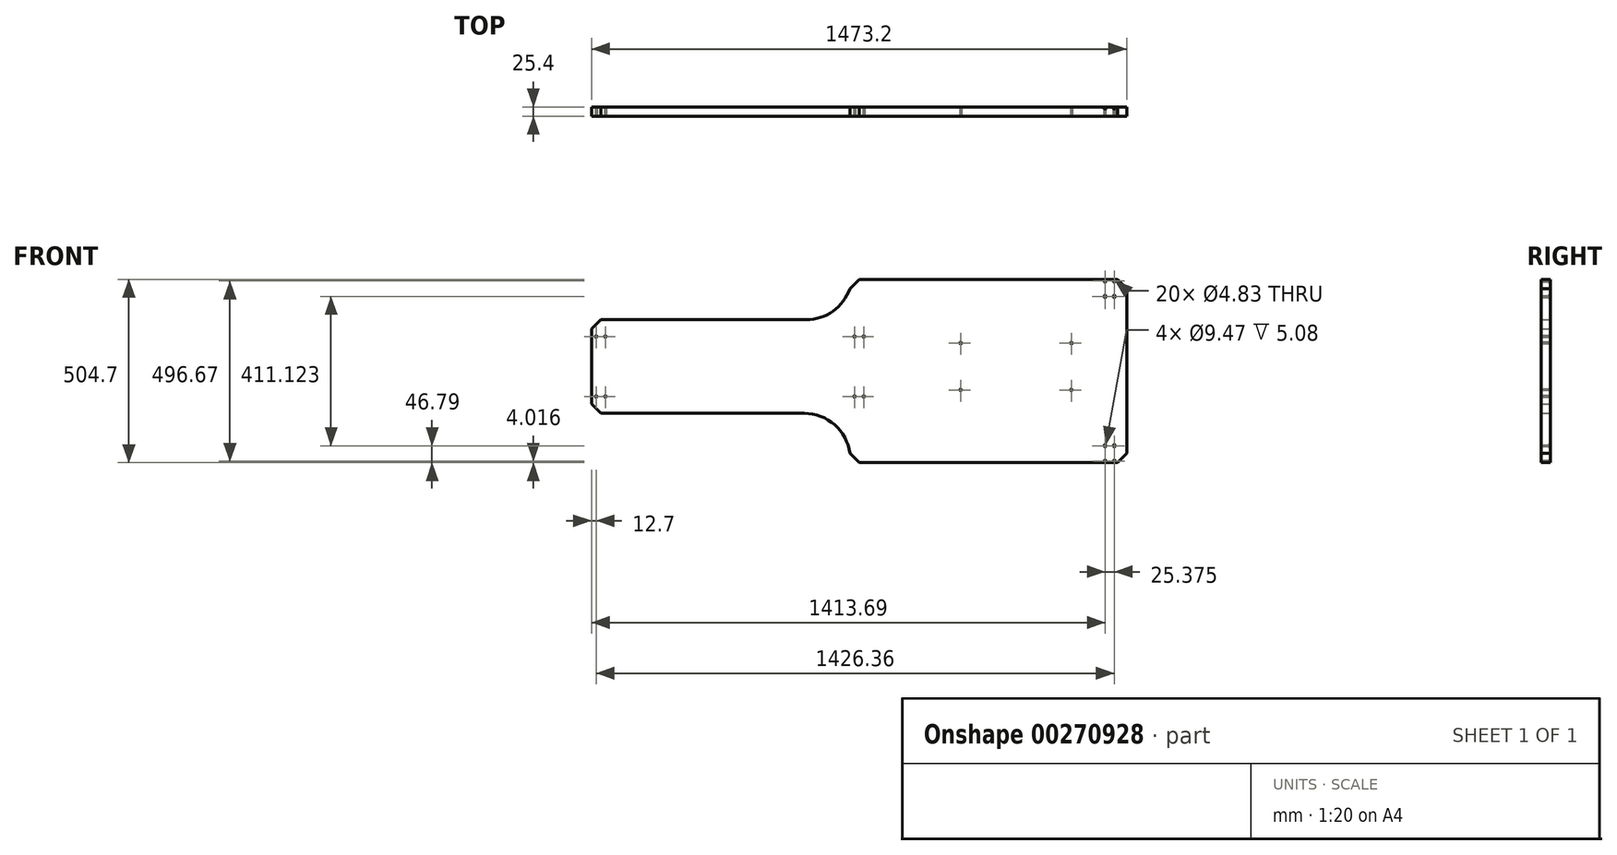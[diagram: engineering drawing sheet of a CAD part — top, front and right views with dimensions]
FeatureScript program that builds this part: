
annotation { "Feature Type Name" : "Feature", "Feature Type Description" : "" }
export const myFeature = defineFeature(function(context is Context, id is Id, definition is map)
    precondition{}
    {
        {
            var Q0;
            Q0=qCreatedBy(makeId("Front.planeOp"),FACE);
            var sketch = newSketch(context, id + "F0", { "sketchPlane" : qUnion([Q0])});
            skLineSegment(sketch, "E0", {"start": v(-1473.2, 384.96) * mm, "end": v(-1473.2, 177.8) * mm});
            skLineSegment(sketch, "E1", {"start": v(-1447.8, 410.36) * mm, "end": v(-881.95, 410.36) * mm});
            skLineSegment(sketch, "E2", {"start": v(-1447.8, 152.4) * mm, "end": v(-887.95, 152.4) * mm});
            skLineSegment(sketch, "E3", {"start": v(-736.6, 16.33) * mm, "end": v(-25.4, 16.33) * mm});
            skLineSegment(sketch, "E4", {"start": v(-736.6, 521.03) * mm, "end": v(-25.4, 521.03) * mm});
            skPoint(sketch, "E5.visualSharp", {"position": v(-762, 410.36) * mm});
            skArc(sketch, "E5.filletArc", {"start": v(-881.95, 410.36) * mm, "mid": v(-808.36, 433.85) * mm, "end": v(-762, 495.63) * mm});
            skPoint(sketch, "E6.visualSharp", {"position": v(-762, 152.4) * mm});
            skArc(sketch, "E6.filletArc", {"start": v(-762, 41.73) * mm, "mid": v(-804.12, 120.8) * mm, "end": v(-887.95, 152.4) * mm});
            skLineSegment(sketch, "E7", {"start": v(-736.6, 521.03) * mm, "end": v(-762, 495.63) * mm});
            skPoint(sketch, "E8.orphan", {"position": v(-762, 521.03) * mm});
            skLineSegment(sketch, "E9", {"start": v(-736.6, 16.33) * mm, "end": v(-762, 41.73) * mm});
            skPoint(sketch, "E10.orphan", {"position": v(-762, 16.33) * mm});
            skLineSegment(sketch, "E11", {"start": v(-25.4, 16.33) * mm, "end": v(0, 41.73) * mm});
            skLineSegment(sketch, "E12", {"start": v(-1473.2, 384.96) * mm, "end": v(-1447.8, 410.36) * mm});
            skLineSegment(sketch, "E13", {"start": v(-1447.8, 152.4) * mm, "end": v(-1473.2, 177.8) * mm});
            skLineSegment(sketch, "E14", {"start": v(0, 495.63) * mm, "end": v(0, 41.73) * mm});
            skPoint(sketch, "E15.endSnap0", {"position": v(0, 140.7) * mm});
            skPoint(sketch, "E16.orphan", {"position": v(-1473.2, 0) * mm});
            skLineSegment(sketch, "E17", {"start": v(-1473.2, 281.38) * mm, "end": v(-1473.2, 344.88) * mm});
            skLineSegment(sketch, "E18", {"start": v(-1473.2, 281.38) * mm, "end": v(-1473.2, 217.88) * mm});
            skLineSegment(sketch, "E19", {"start": v(-1473.2, 344.88) * mm, "end": v(-1473.2, 382.98) * mm});
            skLineSegment(sketch, "E20", {"start": v(-1473.2, 382.98) * mm, "end": v(-1422.4, 382.98) * mm});
            skLineSegment(sketch, "E21", {"start": v(-1473.2, 217.88) * mm, "end": v(-1473.2, 179.78) * mm});
            skLineSegment(sketch, "E22", {"start": v(-1473.2, 179.78) * mm, "end": v(-1422.4, 179.78) * mm});
            skLineSegment(sketch, "E23", {"start": v(-1473.2, 344.88) * mm, "end": v(-711.2, 344.88) * mm});
            skLineSegment(sketch, "E24", {"start": v(-711.2, 344.88) * mm, "end": v(-711.2, 217.88) * mm});
            skLineSegment(sketch, "E25", {"start": v(-711.2, 217.88) * mm, "end": v(-1473.2, 217.88) * mm});
            skLineSegment(sketch, "E26", {"start": v(-1422.4, 179.78) * mm, "end": v(-1422.4, 217.88) * mm});
            skLineSegment(sketch, "E27", {"start": v(-1422.4, 382.98) * mm, "end": v(-1422.4, 344.88) * mm});
            skLineSegment(sketch, "E28", {"start": v(-1473.2, 344.88) * mm, "end": v(-1460.5, 344.88) * mm});
            skLineSegment(sketch, "E29", {"start": v(-1460.5, 344.88) * mm, "end": v(-1460.5, 363.93) * mm});
            skLineSegment(sketch, "E30", {"start": v(-1422.4, 344.88) * mm, "end": v(-1435.1, 344.88) * mm});
            skLineSegment(sketch, "E31", {"start": v(-1435.1, 344.88) * mm, "end": v(-1435.1, 363.93) * mm});
            skLineSegment(sketch, "E32", {"start": v(-1460.5, 217.88) * mm, "end": v(-1460.5, 198.83) * mm});
            skLineSegment(sketch, "E33", {"start": v(-1435.1, 217.88) * mm, "end": v(-1435.1, 198.83) * mm});
            skLineSegment(sketch, "E34", {"start": v(-711.2, 217.88) * mm, "end": v(-723.9, 217.88) * mm});
            skLineSegment(sketch, "E35", {"start": v(-723.9, 217.88) * mm, "end": v(-723.9, 198.83) * mm});
            skLineSegment(sketch, "E36", {"start": v(-762, 198.83) * mm, "end": v(-762, 217.88) * mm});
            skLineSegment(sketch, "E37", {"start": v(-711.2, 344.88) * mm, "end": v(-723.9, 344.88) * mm});
            skLineSegment(sketch, "E38", {"start": v(-723.9, 344.88) * mm, "end": v(-762, 344.88) * mm});
            skLineSegment(sketch, "E39", {"start": v(-762, 344.88) * mm, "end": v(-762, 363.93) * mm});
            skLineSegment(sketch, "E40", {"start": v(-723.9, 344.88) * mm, "end": v(-723.9, 363.93) * mm});
            skLineSegment(sketch, "E41", {"start": v(0, 495.63) * mm, "end": v(-25.4, 521.03) * mm});
            skSolve(sketch);
        }
        {
            var Q0;
            Q0=makeQuery(id+"F0.imprint","IMPRINT",FACE,{"disambiguationData":[TD([[makeQuery(id+"F0.imprint","IMPRINT",EDGE,{"derivedFrom":sQuery(id+"F0.wireOp",EDGE,"E0")}),1.0]])]});
            extrude(context, id + "F1", {"entities" : qUnion([Q0]), "depth" : 12.7 * mm});
        }
        {
            var Q0;
            Q0=makeQuery(id+"F1.opExtrude","CAP_FACE",FACE,{"disambiguationData":[OSD([sQuery(id+"F0.wireOp",EDGE,"E0"),sQuery(id+"F0.wireOp",EDGE,"E1"),sQuery(id+"F0.wireOp",EDGE,"E2"),sQuery(id+"F0.wireOp",EDGE,"E3"),sQuery(id+"F0.wireOp",EDGE,"E4"),sQuery(id+"F0.wireOp",EDGE,"E5.filletArc"),sQuery(id+"F0.wireOp",EDGE,"E6.filletArc"),sQuery(id+"F0.wireOp",EDGE,"E7"),sQuery(id+"F0.wireOp",EDGE,"E9"),sQuery(id+"F0.wireOp",EDGE,"E11"),sQuery(id+"F0.wireOp",EDGE,"2SLSGWGz-MLWY-dJ0c-EU9p-pr2KKDG8ahuz"),sQuery(id+"F0.wireOp",EDGE,"E12"),sQuery(id+"F0.wireOp",EDGE,"E13"),sQuery(id+"F0.wireOp",EDGE,"E14"),sQuery(id+"F0.wireOp",EDGE,"1ipnpV95-zsMA-DrG2-5ojF-kC9brwyhWKc4")])],"isStart":false});
            var sketch = newSketch(context, id + "F2", { "sketchPlane" : qUnion([Q0])});
            skLineSegment(sketch, "E42", {"start": v(-25.4, 16.33) * mm, "end": v(0, 0) * mm});
            skLineSegment(sketch, "E43", {"start": v(0, 0) * mm, "end": v(0, 562.76) * mm});
            skLineSegment(sketch, "E44", {"start": v(0, 562.76) * mm, "end": v(-736.6, 521.03) * mm});
            skLineSegment(sketch, "E45", {"start": v(0, 562.76) * mm, "end": v(0, 268.68) * mm});
            skLineSegment(sketch, "E46", {"start": v(0, 0) * mm, "end": v(0, 268.68) * mm});
            skLineSegment(sketch, "E47", {"start": v(0, 0) * mm, "end": v(0, 134.34) * mm});
            skLineSegment(sketch, "E48", {"start": v(0, 134.34) * mm, "end": v(-152.4, 134.34) * mm});
            skLineSegment(sketch, "E49", {"start": v(-152.4, 134.34) * mm, "end": v(-457.2, 134.34) * mm});
            skLineSegment(sketch, "E50", {"start": v(0, 562.76) * mm, "end": v(0, 415.72) * mm});
            skLineSegment(sketch, "E51", {"start": v(0, 415.72) * mm, "end": v(-152.4, 415.72) * mm});
            skLineSegment(sketch, "E52", {"start": v(-152.4, 415.72) * mm, "end": v(-457.2, 415.72) * mm});
            skPoint(sketch, "E53", {"position": v(-457.2, 415.72) * mm});
            skPoint(sketch, "E54", {"position": v(-152.4, 415.72) * mm});
            skPoint(sketch, "E55", {"position": v(-457.2, 134.34) * mm});
            skPoint(sketch, "E56", {"position": v(-152.4, 134.34) * mm});
            skSolve(sketch);
        }
        {
            var Q0;
            Q0=sQuery(id+"F2.wireOp",VERTEX,"E53");
            var Q1;
            Q1=sQuery(id+"F2.wireOp",VERTEX,"E54");
            var Q2;
            Q2=sQuery(id+"F2.wireOp",VERTEX,"E56");
            var Q3;
            Q3=sQuery(id+"F2.wireOp",VERTEX,"E55");
            var Q4;
            Q4=makeQuery(id+"F1.opExtrude","SWEPT_BODY",BODY,{"disambiguationData":[OSD([sQuery(id+"F0.wireOp",EDGE,"E0"),sQuery(id+"F0.wireOp",EDGE,"E1"),sQuery(id+"F0.wireOp",EDGE,"E2"),sQuery(id+"F0.wireOp",EDGE,"E3"),sQuery(id+"F0.wireOp",EDGE,"E4"),sQuery(id+"F0.wireOp",EDGE,"E5.filletArc"),sQuery(id+"F0.wireOp",EDGE,"E6.filletArc"),sQuery(id+"F0.wireOp",EDGE,"E7"),sQuery(id+"F0.wireOp",EDGE,"E9"),sQuery(id+"F0.wireOp",EDGE,"E11"),sQuery(id+"F0.wireOp",EDGE,"2SLSGWGz-MLWY-dJ0c-EU9p-pr2KKDG8ahuz"),sQuery(id+"F0.wireOp",EDGE,"E12"),sQuery(id+"F0.wireOp",EDGE,"E13"),sQuery(id+"F0.wireOp",EDGE,"E14"),sQuery(id+"F0.wireOp",EDGE,"1ipnpV95-zsMA-DrG2-5ojF-kC9brwyhWKc4")])]});
            hole(context, id + "F3", {"style" : HoleStyle.SIMPLE, "endStyle" : HoleEndStyle.THROUGH, "holeDiameter" : 4.83 * mm, "tappedDepth" : 12.7 * mm, "tapClearance" : 3, "locations" : qUnion([Q0, Q1, Q2, Q3]), "scope" : qUnion([Q4])});
        }
        {
            var Q0;
            Q0 = qSketchRegion(id + "F0", true);
            extrude(context, id + "F4", {"entities" : qUnion([Q0]), "operationType" : NewBodyOperationType.ADD, "depth" : 25.4 * mm});
        }
        {
            var Q0;
            Q0=makeQuery(id+"F4.opExtrude","CAP_FACE",FACE,{"disambiguationData":[OSD([sQuery(id+"F0.wireOp",EDGE,"E0"),sQuery(id+"F0.wireOp",EDGE,"E1"),sQuery(id+"F0.wireOp",EDGE,"E2"),sQuery(id+"F0.wireOp",EDGE,"E3"),sQuery(id+"F0.wireOp",EDGE,"E4"),sQuery(id+"F0.wireOp",EDGE,"E5.filletArc"),sQuery(id+"F0.wireOp",EDGE,"E6.filletArc"),sQuery(id+"F0.wireOp",EDGE,"E7"),sQuery(id+"F0.wireOp",EDGE,"E9"),sQuery(id+"F0.wireOp",EDGE,"E11"),sQuery(id+"F0.wireOp",EDGE,"2SLSGWGz-MLWY-dJ0c-EU9p-pr2KKDG8ahuz"),sQuery(id+"F0.wireOp",EDGE,"E12"),sQuery(id+"F0.wireOp",EDGE,"E13"),sQuery(id+"F0.wireOp",EDGE,"E14"),sQuery(id+"F0.wireOp",EDGE,"1ipnpV95-zsMA-DrG2-5ojF-kC9brwyhWKc4"),sQuery(id+"F0.wireOp",EDGE,"E17"),sQuery(id+"F0.wireOp",EDGE,"E18"),sQuery(id+"F0.wireOp",EDGE,"E19"),sQuery(id+"F0.wireOp",EDGE,"E21")])],"isStart":false});
            var sketch = newSketch(context, id + "F5", { "sketchPlane" : qUnion([Q0])});
            skLineSegment(sketch, "E57", {"start": v(-1473.2, 281.38) * mm, "end": v(-711.2, 281.38) * mm});
            skLineSegment(sketch, "E58", {"start": v(-711.2, 281.38) * mm, "end": v(-711.2, 217.88) * mm});
            skLineSegment(sketch, "E59", {"start": v(-711.2, 217.88) * mm, "end": v(-723.9, 217.88) * mm});
            skLineSegment(sketch, "E60", {"start": v(-723.9, 217.88) * mm, "end": v(-723.9, 198.83) * mm});
            skLineSegment(sketch, "E61", {"start": v(-1473.2, 281.38) * mm, "end": v(-1473.2, 217.88) * mm});
            skLineSegment(sketch, "E62", {"start": v(-1473.2, 217.88) * mm, "end": v(-1422.4, 217.88) * mm});
            skLineSegment(sketch, "E63", {"start": v(-1422.4, 217.88) * mm, "end": v(-1435.1, 217.88) * mm});
            skPoint(sketch, "E63.endSnap0", {"position": v(-1447.8, 217.88) * mm});
            skLineSegment(sketch, "E64", {"start": v(-1435.1, 217.88) * mm, "end": v(-1435.1, 198.83) * mm});
            skLineSegment(sketch, "E65", {"start": v(-1460.5, 198.83) * mm, "end": v(-1460.5, 217.88) * mm});
            skLineSegment(sketch, "E66", {"start": v(-749.3, 217.88) * mm, "end": v(-749.3, 198.83) * mm});
            skLineSegment(sketch, "E67.MirrorCS", {"start": v(-749.3, 344.88) * mm, "end": v(-749.3, 363.93) * mm});
            skLineSegment(sketch, "E68.MirrorCS", {"start": v(-723.9, 344.88) * mm, "end": v(-723.9, 363.93) * mm});
            skLineSegment(sketch, "E69.MirrorCS", {"start": v(-1435.1, 344.88) * mm, "end": v(-1435.1, 363.93) * mm});
            skLineSegment(sketch, "E70.MirrorCS", {"start": v(-1460.5, 363.93) * mm, "end": v(-1460.5, 344.88) * mm});
            skSolve(sketch);
        }
        {
            var Q0;
            Q0=makeQuery(id+"F4.opExtrude","CAP_FACE",FACE,{"disambiguationData":[OSD([sQuery(id+"F0.wireOp",EDGE,"E0"),sQuery(id+"F0.wireOp",EDGE,"E1"),sQuery(id+"F0.wireOp",EDGE,"E2"),sQuery(id+"F0.wireOp",EDGE,"E3"),sQuery(id+"F0.wireOp",EDGE,"E4"),sQuery(id+"F0.wireOp",EDGE,"E5.filletArc"),sQuery(id+"F0.wireOp",EDGE,"E6.filletArc"),sQuery(id+"F0.wireOp",EDGE,"E7"),sQuery(id+"F0.wireOp",EDGE,"E9"),sQuery(id+"F0.wireOp",EDGE,"E11"),sQuery(id+"F0.wireOp",EDGE,"E12"),sQuery(id+"F0.wireOp",EDGE,"E13"),sQuery(id+"F0.wireOp",EDGE,"E14"),sQuery(id+"F0.wireOp",EDGE,"E17"),sQuery(id+"F0.wireOp",EDGE,"E18"),sQuery(id+"F0.wireOp",EDGE,"E19"),sQuery(id+"F0.wireOp",EDGE,"E21"),sQuery(id+"F0.wireOp",EDGE,"E41")])],"isStart":false});
            var sketch = newSketch(context, id + "F6", { "sketchPlane" : qUnion([Q0])});
            skLineSegment(sketch, "E71", {"start": v(-1447.8, 410.36) * mm, "end": v(-1473.2, 410.36) * mm});
            skLineSegment(sketch, "E72", {"start": v(-1473.2, 177.8) * mm, "end": v(-1473.2, 152.4) * mm});
            skLineSegment(sketch, "E73", {"start": v(-1447.8, 152.4) * mm, "end": v(-1473.2, 152.4) * mm});
            skLineSegment(sketch, "E74", {"start": v(-1473.2, 410.36) * mm, "end": v(0, 410.36) * mm});
            skLineSegment(sketch, "E75", {"start": v(-1473.2, 152.4) * mm, "end": v(0, 152.4) * mm});
            skLineSegment(sketch, "E76", {"start": v(0, 410.36) * mm, "end": v(0, 281.38) * mm});
            skLineSegment(sketch, "E77", {"start": v(0, 152.4) * mm, "end": v(0, 281.38) * mm});
            skLineSegment(sketch, "E78", {"start": v(0, 410.36) * mm, "end": v(0, 345.87) * mm});
            skLineSegment(sketch, "E79", {"start": v(0, 152.4) * mm, "end": v(0, 216.9) * mm});
            skLineSegment(sketch, "E80", {"start": v(-152.4, 216.9) * mm, "end": v(-152.4, 152.4) * mm});
            skLineSegment(sketch, "E81", {"start": v(-152.4, 345.87) * mm, "end": v(-152.4, 410.36) * mm});
            skLineSegment(sketch, "E82", {"start": v(0, 410.36) * mm, "end": v(-457.2, 410.36) * mm});
            skLineSegment(sketch, "E83", {"start": v(-457.2, 410.36) * mm, "end": v(-457.2, 345.87) * mm});
            skLineSegment(sketch, "E84", {"start": v(-457.2, 216.9) * mm, "end": v(-457.2, 152.4) * mm});
            skSolve(sketch);
        }
        {
            var Q0;
            Q0=sQuery(id+"F5.wireOp",VERTEX,"E70.MirrorCS.start");
            var Q1;
            Q1=sQuery(id+"F5.wireOp",VERTEX,"E69.MirrorCS.end");
            var Q2;
            Q2=sQuery(id+"F5.wireOp",VERTEX,"E64.end");
            var Q3;
            Q3=sQuery(id+"F5.wireOp",VERTEX,"E65.start");
            var Q4;
            Q4=sQuery(id+"F5.wireOp",VERTEX,"E66.end");
            var Q5;
            Q5=sQuery(id+"F5.wireOp",VERTEX,"E60.end");
            var Q6;
            Q6=sQuery(id+"F5.wireOp",VERTEX,"E67.MirrorCS.end");
            var Q7;
            Q7=sQuery(id+"F5.wireOp",VERTEX,"E68.MirrorCS.end");
            var Q8;
            Q8=sQuery(id+"F6.wireOp",VERTEX,"E83.end");
            var Q9;
            Q9=sQuery(id+"F6.wireOp",VERTEX,"E81.start");
            var Q10;
            Q10=sQuery(id+"F6.wireOp",VERTEX,"E80.start");
            var Q11;
            Q11=sQuery(id+"F6.wireOp",VERTEX,"E84.start");
            var Q12;
            Q12=makeQuery(id+"F1.opExtrude","SWEPT_BODY",BODY,{"disambiguationData":[OSD([sQuery(id+"F0.wireOp",EDGE,"E0"),sQuery(id+"F0.wireOp",EDGE,"E1"),sQuery(id+"F0.wireOp",EDGE,"E2"),sQuery(id+"F0.wireOp",EDGE,"E3"),sQuery(id+"F0.wireOp",EDGE,"E4"),sQuery(id+"F0.wireOp",EDGE,"E5.filletArc"),sQuery(id+"F0.wireOp",EDGE,"E6.filletArc"),sQuery(id+"F0.wireOp",EDGE,"E7"),sQuery(id+"F0.wireOp",EDGE,"E9"),sQuery(id+"F0.wireOp",EDGE,"E11"),sQuery(id+"F0.wireOp",EDGE,"2SLSGWGz-MLWY-dJ0c-EU9p-pr2KKDG8ahuz"),sQuery(id+"F0.wireOp",EDGE,"E12"),sQuery(id+"F0.wireOp",EDGE,"E13"),sQuery(id+"F0.wireOp",EDGE,"E14"),sQuery(id+"F0.wireOp",EDGE,"1ipnpV95-zsMA-DrG2-5ojF-kC9brwyhWKc4"),sQuery(id+"F0.wireOp",EDGE,"E20"),sQuery(id+"F0.wireOp",EDGE,"E22"),sQuery(id+"F0.wireOp",EDGE,"E23"),sQuery(id+"F0.wireOp",EDGE,"E24"),sQuery(id+"F0.wireOp",EDGE,"E25"),sQuery(id+"F0.wireOp",EDGE,"E26"),sQuery(id+"F0.wireOp",EDGE,"E27"),sQuery(id+"F0.wireOp",EDGE,"E34"),sQuery(id+"F0.wireOp",EDGE,"E37"),sQuery(id+"F0.wireOp",EDGE,"E38")])]});
            hole(context, id + "F7", {"style" : HoleStyle.SIMPLE, "endStyle" : HoleEndStyle.THROUGH, "holeDiameter" : 4.83 * mm, "tappedDepth" : 12.7 * mm, "tapClearance" : 3, "locations" : qUnion([Q0, Q1, Q2, Q3, Q4, Q5, Q6, Q7, Q8, Q9, Q10, Q11]), "scope" : qUnion([Q12])});
        }
        {
            var Q0;
            Q0=makeQuery(id+"F0.imprint","IMPRINT",FACE,{"disambiguationData":[TD([[makeQuery(id+"F0.imprint","IMPRINT",EDGE,{"derivedFrom":sQuery(id+"F0.wireOp",EDGE,"E1")}),-1.0]])]});
            var sketch = newSketch(context, id + "F8", { "sketchPlane" : qUnion([Q0])});
            skLineSegment(sketch, "E85", {"start": v(-25.4, 16.33) * mm, "end": v(-25.4, 20.35) * mm});
            skLineSegment(sketch, "E86", {"start": v(-25.4, 16.33) * mm, "end": v(-68.25, 16.33) * mm});
            skLineSegment(sketch, "E87", {"start": v(-25.4, 20.35) * mm, "end": v(-34.14, 20.35) * mm});
            skLineSegment(sketch, "E88", {"start": v(-68.25, 16.33) * mm, "end": v(-68.25, 20.35) * mm});
            skLineSegment(sketch, "E89", {"start": v(-68.25, 20.35) * mm, "end": v(-59.51, 20.35) * mm});
            skLineSegment(sketch, "E90", {"start": v(-68.25, 16.33) * mm, "end": v(-68.25, 67.13) * mm});
            skLineSegment(sketch, "E91", {"start": v(-68.25, 67.13) * mm, "end": v(-25.4, 67.13) * mm});
            skLineSegment(sketch, "E92", {"start": v(-25.4, 67.13) * mm, "end": v(-25.4, 63.12) * mm});
            skLineSegment(sketch, "E93", {"start": v(-25.4, 63.12) * mm, "end": v(-34.14, 63.12) * mm});
            skLineSegment(sketch, "E94", {"start": v(-68.25, 67.13) * mm, "end": v(-68.25, 63.12) * mm});
            skLineSegment(sketch, "E95", {"start": v(-68.25, 63.12) * mm, "end": v(-59.51, 63.12) * mm});
            skLineSegment(sketch, "E96", {"start": v(-25.4, 470.23) * mm, "end": v(-68.25, 470.23) * mm});
            skLineSegment(sketch, "E97", {"start": v(-68.25, 470.23) * mm, "end": v(-68.25, 474.24) * mm});
            skLineSegment(sketch, "E98", {"start": v(-68.25, 474.24) * mm, "end": v(-59.51, 474.24) * mm});
            skLineSegment(sketch, "E99", {"start": v(-25.4, 470.23) * mm, "end": v(-25.4, 474.24) * mm});
            skLineSegment(sketch, "E100", {"start": v(-25.4, 474.24) * mm, "end": v(-34.14, 474.24) * mm});
            skLineSegment(sketch, "E101", {"start": v(-25.4, 517.02) * mm, "end": v(-34.14, 517.02) * mm});
            skLineSegment(sketch, "E102", {"start": v(-25.4, 521.03) * mm, "end": v(-68.25, 521.03) * mm});
            skLineSegment(sketch, "E103", {"start": v(-68.25, 521.03) * mm, "end": v(-68.25, 517.02) * mm});
            skLineSegment(sketch, "E104", {"start": v(-68.25, 517.02) * mm, "end": v(-59.51, 517.02) * mm});
            skSolve(sketch);
        }
        {
            var Q0;
            Q0=sQuery(id+"F8.wireOp",VERTEX,"E93.end");
            var Q1;
            Q1=sQuery(id+"F8.wireOp",VERTEX,"E95.end");
            var Q2;
            Q2=sQuery(id+"F8.wireOp",VERTEX,"E87.end");
            var Q3;
            Q3=sQuery(id+"F8.wireOp",VERTEX,"E89.end");
            var Q4;
            Q4=sQuery(id+"F8.wireOp",VERTEX,"E104.end");
            var Q5;
            Q5=sQuery(id+"F8.wireOp",VERTEX,"E101.end");
            var Q6;
            Q6=sQuery(id+"F8.wireOp",VERTEX,"E100.end");
            var Q7;
            Q7=sQuery(id+"F8.wireOp",VERTEX,"E98.end");
            var Q8;
            Q8=makeQuery(id+"F1.opExtrude","SWEPT_BODY",BODY,{"disambiguationData":[OSD([sQuery(id+"F0.wireOp",EDGE,"E0"),sQuery(id+"F0.wireOp",EDGE,"E1"),sQuery(id+"F0.wireOp",EDGE,"E2"),sQuery(id+"F0.wireOp",EDGE,"E3"),sQuery(id+"F0.wireOp",EDGE,"E4"),sQuery(id+"F0.wireOp",EDGE,"E5.filletArc"),sQuery(id+"F0.wireOp",EDGE,"E6.filletArc"),sQuery(id+"F0.wireOp",EDGE,"E7"),sQuery(id+"F0.wireOp",EDGE,"E9"),sQuery(id+"F0.wireOp",EDGE,"E11"),sQuery(id+"F0.wireOp",EDGE,"E12"),sQuery(id+"F0.wireOp",EDGE,"E13"),sQuery(id+"F0.wireOp",EDGE,"E14"),sQuery(id+"F0.wireOp",EDGE,"E20"),sQuery(id+"F0.wireOp",EDGE,"E22"),sQuery(id+"F0.wireOp",EDGE,"E23"),sQuery(id+"F0.wireOp",EDGE,"E24"),sQuery(id+"F0.wireOp",EDGE,"E25"),sQuery(id+"F0.wireOp",EDGE,"E26"),sQuery(id+"F0.wireOp",EDGE,"E27"),sQuery(id+"F0.wireOp",EDGE,"E34"),sQuery(id+"F0.wireOp",EDGE,"E37"),sQuery(id+"F0.wireOp",EDGE,"E38"),sQuery(id+"F0.wireOp",EDGE,"E41")])]});
            hole(context, id + "F9", {"style" : HoleStyle.C_BORE, "endStyle" : HoleEndStyle.THROUGH, "oppositeDirection" : true, "holeDiameter" : 4.83 * mm, "cBoreDiameter" : 9.47 * mm, "cBoreDepth" : 5.08 * mm, "tappedDepth" : 12.7 * mm, "tapClearance" : 3, "locations" : qUnion([Q0, Q1, Q2, Q3, Q4, Q5, Q6, Q7]), "scope" : qUnion([Q8])});
        }
    });
